# Revit family: BDG_BossDesign_PnlPrttns_Aspect2
name_source: partatom
category: Furniture Systems
revit_build: Autodesk Revit 2015 (Build: 20140903_1530(x64)
units: mm (PartAtom-declared; Revit-internal decimal feet)

## types (1)
- BDG_BossDesign_PnlPrttns_Aspect2
    Assembly Code = E2020
    AssetType = Movable
    BIMObjectName = BDG_BossDesign_PanelPartitions_Aspect2
    Category = Ss_25_10_30 : Framed partition systems
    Description = Aspect 2 3000 x 1700 x 2275mm
    DurationUnit = year
    ExpectedLife = 5
    IfcExportAs = IfcFurnishingElementType
    IfcExportType = FRAMED PARTITION SYSTEMS
    Keynote = Ss_25_10_30
    ManufacturerName = Boss Design
    ManufacturerURL = www.bossdesign.com
    Material = Aluminium frame
    Model = Aspect 2
    ModelNumber = Aspect 2
    ModelReference = Aspect 2 3000 x 1700 x 2275mm
    NBSDescription = Panel partitions
    NBSReference = 45-35-80/420
    Name = PanelPartitions_Aspect2_BossDesign
    NominalHeight = 2275 mm
    NominalLength = 3000 mm  [stored 9.84252 ft]
    NominalWidth = 1700 mm  [stored 5.57743 ft]
    ProductInformation = www.bossdesign.com/product-list/aspect-2/
    Revision = 1
    Shape = Rectangular
    Size = 3000 x 1700 x 2275mm
    URL = www.bossdesign.com
    Uniclass2015Description = Framed partition systems
    Uniclass2015Reference = Ss_25_10_30
    Uniclass2015Version = Products v1.9
    UpholsteredPanelMaterial = BDG_Camira_Fabric_Lucia-AdoboYB165
    Version = 1
    WarrantyDescription = Structural Warranty Excludes Foams and Fabrics
    WarrantyDurationLabor = 5
    WarrantyDurationParts = 5
    WarrantyDurationUnit = year

note: [stored X ft] marks values corroborated as IEEE doubles in the binary element streams (Revit-internal decimal feet)

## geometry (parser evidence)
native form markers: Sweep x2
no freeform markers — native parametric forms only
